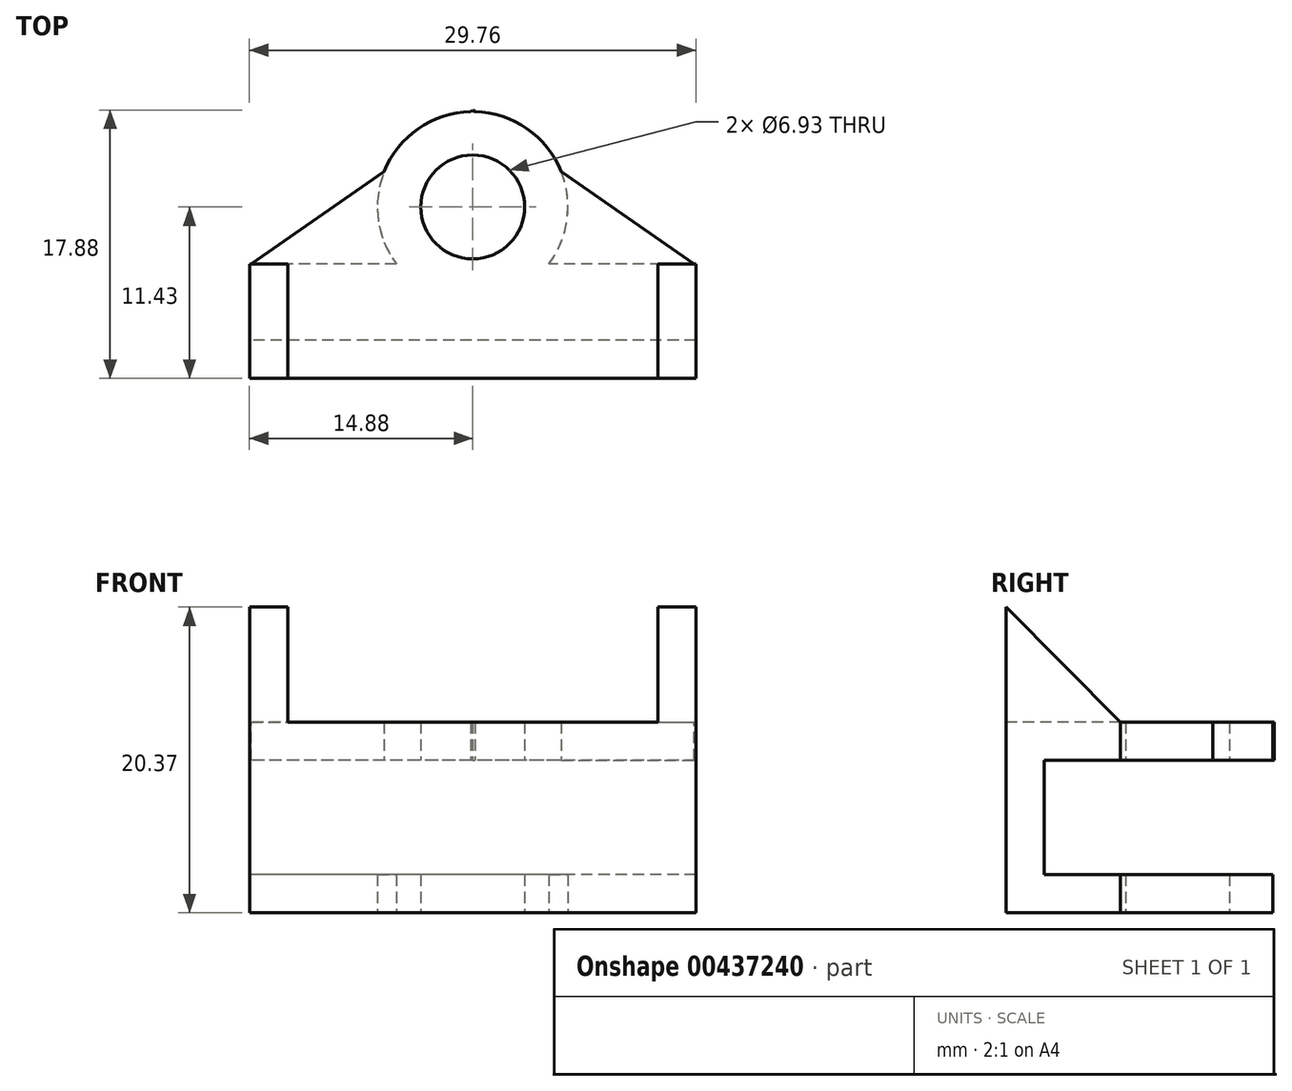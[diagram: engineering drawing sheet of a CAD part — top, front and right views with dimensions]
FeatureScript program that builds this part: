
annotation { "Feature Type Name" : "Feature", "Feature Type Description" : "" }
export const myFeature = defineFeature(function(context is Context, id is Id, definition is map)
    precondition{}
    {
        {
            var Q0;
            Q0=qCreatedBy(makeId("Top.planeOp"),FACE);
            var sketch = newSketch(context, id + "F0", { "sketchPlane" : qUnion([Q0])});
            skCircle(sketch, "E0", {"center": v(0, 0) * mm, "radius": 6.35 * mm});
            skSolve(sketch);
        }
        {
            var Q0;
            Q0=makeQuery(id+"F0.imprint","IMPRINT",FACE,{"disambiguationData":[TD([[makeQuery(id+"F0.imprint","IMPRINT",EDGE,{"derivedFrom":sQuery(id+"F0.wireOp",EDGE,"E0")}),1.0]])]});
            var Q1;
            Q1=sQuery(id+"F0.wireOp",EDGE,"E0");
            extrude(context, id + "F1", {"entities" : qUnion([Q0]), "surfaceEntities" : qUnion([Q1]), "endBound" : BoundingType.SYMMETRIC, "depth" : 12.7 * mm});
        }
        {
            var Q0;
            Q0=qCreatedBy(makeId("Top.planeOp"),FACE);
            var sketch = newSketch(context, id + "F2", { "sketchPlane" : qUnion([Q0])});
            skCircle(sketch, "E1", {"center": v(0, 0) * mm, "radius": 6.35 * mm});
            skSolve(sketch);
        }
        {
            var Q0;
            Q0 = qSketchRegion(id + "F2", true);
            extrude(context, id + "F3", {"entities" : qUnion([Q0]), "operationType" : NewBodyOperationType.REMOVE, "endBound" : BoundingType.SYMMETRIC, "oppositeDirection" : true, "depth" : 7.62 * mm});
        }
        {
            var Q0;
            Q0=qCreatedBy(makeId("Top.planeOp"),FACE);
            var sketch = newSketch(context, id + "F4", { "sketchPlane" : qUnion([Q0])});
            skLineSegment(sketch, "E2.bottom", {"start": v(0, -3.81) * mm, "end": v(-14.88, -3.81) * mm});
            skLineSegment(sketch, "E2.top", {"start": v(0, -11.43) * mm, "end": v(-14.88, -11.43) * mm});
            skLineSegment(sketch, "E2.left", {"start": v(0, -3.81) * mm, "end": v(0, -11.43) * mm});
            skLineSegment(sketch, "E2.right", {"start": v(-14.88, -3.81) * mm, "end": v(-14.88, -11.43) * mm});
            skLineSegment(sketch, "E3.MirrorCS", {"start": v(0, -11.43) * mm, "end": v(14.88, -11.43) * mm});
            skLineSegment(sketch, "E4.MirrorCS", {"start": v(14.88, -3.81) * mm, "end": v(14.88, -11.43) * mm});
            skLineSegment(sketch, "E5.MirrorCS", {"start": v(0, -3.81) * mm, "end": v(14.88, -3.81) * mm});
            skSolve(sketch);
        }
        {
            var Q0;
            Q0 = qSketchRegion(id + "F4", true);
            extrude(context, id + "F5", {"entities" : qUnion([Q0]), "operationType" : NewBodyOperationType.ADD, "endBound" : BoundingType.SYMMETRIC, "depth" : 12.7 * mm});
        }
        {
            var Q0;
            Q0=makeQuery(id+"F5.opExtrude","SWEPT_FACE",FACE,{"disambiguationData":[OSD([sQuery(id+"F4.wireOp",EDGE,"E2.bottom"),sQuery(id+"F4.wireOp",EDGE,"E5.MirrorCS")])]});
            var Q1;
            Q1=makeQuery(id+"F5.opExtrude","SWEPT_FACE",FACE,{"disambiguationData":[OSD([sQuery(id+"F4.wireOp",EDGE,"E2.right")])]});
            var Q2;
            Q2=makeQuery(id+"F5.opExtrude","SWEPT_FACE",FACE,{"disambiguationData":[OSD([sQuery(id+"F4.wireOp",EDGE,"E4.MirrorCS")])]});
            shell(context, id + "F6", {"entities" : qUnion([Q0, Q1, Q2]), "thickness" : 2.54 * mm});
        }
        {
            var Q0;
            Q0=makeQuery(id+"F5.opExtrude","SWEPT_FACE",FACE,{"disambiguationData":[OSD([sQuery(id+"F4.wireOp",EDGE,"E4.MirrorCS")])]});
            var sketch = newSketch(context, id + "F7", { "sketchPlane" : qUnion([Q0])});
            skLineSegment(sketch, "E6", {"start": v(-11.43, 6.35) * mm, "end": v(-11.43, 14.02) * mm});
            skLineSegment(sketch, "E7", {"start": v(-11.43, 14.02) * mm, "end": v(-3.81, 6.35) * mm});
            skLineSegment(sketch, "E8", {"start": v(-3.81, 6.35) * mm, "end": v(-11.43, 6.35) * mm});
            skSolve(sketch);
        }
        {
            var Q0;
            Q0 = qSketchRegion(id + "F7", true);
            extrude(context, id + "F8", {"entities" : qUnion([Q0]), "operationType" : NewBodyOperationType.ADD, "oppositeDirection" : true, "depth" : 2.54 * mm});
        }
        {
            var Q0;
            Q0=makeQuery(id+"F3.boolean.opBoolean","SPLIT",BODY,{"disambiguationData":[OD(0.0)],"derivedFrom":makeQuery(id+"F1.opExtrude","SWEPT_BODY",BODY,{"disambiguationData":[OSD([sQuery(id+"F0.wireOp",EDGE,"E0")])]})});
            var Q1;
            Q1=qCreatedBy(makeId("Right.planeOp"),FACE);
            mirror(context, id + "F9", {"operationType" : NewBodyOperationType.ADD, "entities" : qUnion([Q0]), "mirrorPlane" : qUnion([Q1])});
        }
        {
            var Q0;
            Q0=qCreatedBy(makeId("Top.planeOp"),FACE);
            var sketch = newSketch(context, id + "F10", { "sketchPlane" : qUnion([Q0])});
            skLineSegment(sketch, "E9", {"start": v(0, 6.45) * mm, "end": v(-14.78, -3.82) * mm});
            skLineSegment(sketch, "E10", {"start": v(-14.78, -3.82) * mm, "end": v(0, -3.82) * mm});
            skLineSegment(sketch, "E11", {"start": v(0, -3.82) * mm, "end": v(0, 6.45) * mm});
            skLineSegment(sketch, "E12.MirrorCS", {"start": v(0, 6.45) * mm, "end": v(14.78, -3.82) * mm});
            skLineSegment(sketch, "E13.MirrorCS", {"start": v(14.78, -3.82) * mm, "end": v(0, -3.82) * mm});
            skSolve(sketch);
        }
        {
            var Q0;
            Q0 = qSketchRegion(id + "F10", true);
            extrude(context, id + "F11", {"entities" : qUnion([Q0]), "operationType" : NewBodyOperationType.ADD, "depth" : 6.35 * mm, "hasSecondDirection" : true, "secondDirectionOppositeDirection" : true, "secondDirectionDepth" : -3.8 * mm});
        }
        {
            var Q0;
            Q0=qCreatedBy(makeId("Top.planeOp"),FACE);
            var sketch = newSketch(context, id + "F12", { "sketchPlane" : qUnion([Q0])});
            skCircle(sketch, "E14", {"center": v(0, 0) * mm, "radius": 3.47 * mm});
            skSolve(sketch);
        }
        {
            var Q0;
            Q0 = qSketchRegion(id + "F12", true);
            extrude(context, id + "F13", {"entities" : qUnion([Q0]), "operationType" : NewBodyOperationType.REMOVE, "endBound" : BoundingType.SYMMETRIC, "depth" : 25.4 * mm});
        }
    });
